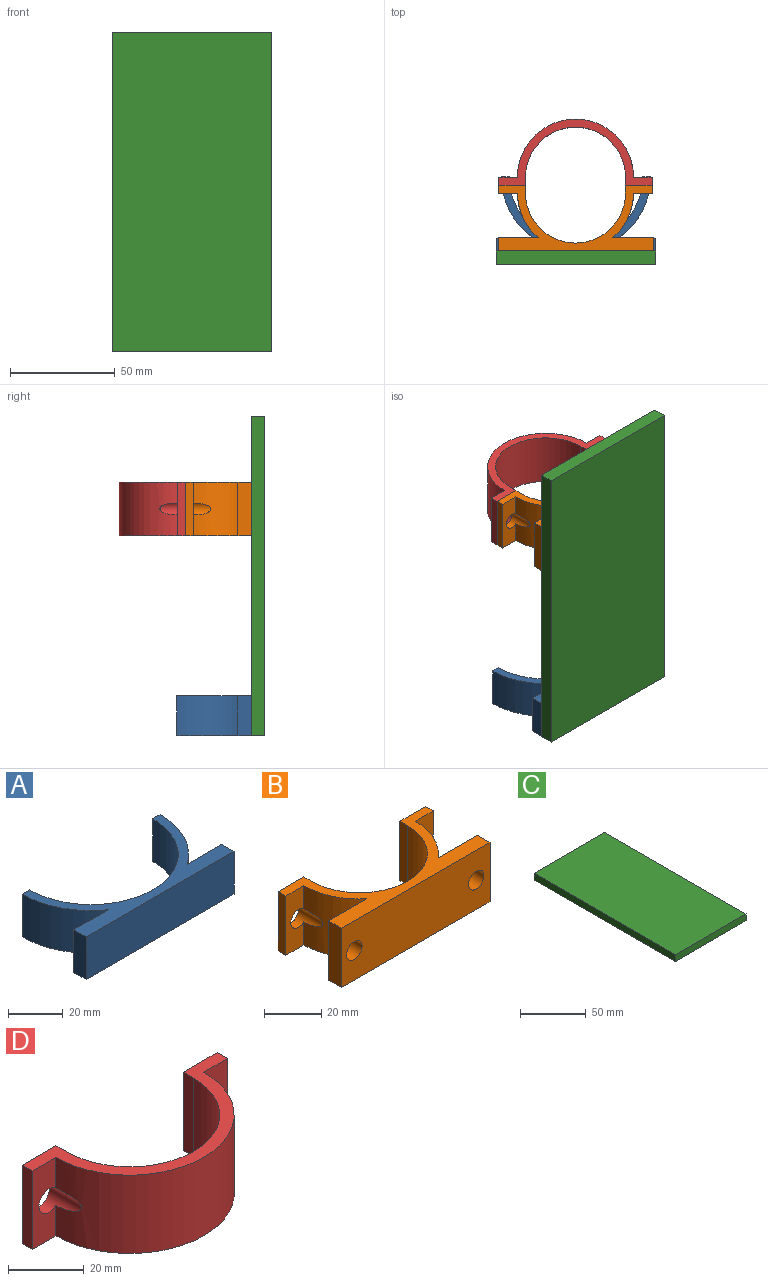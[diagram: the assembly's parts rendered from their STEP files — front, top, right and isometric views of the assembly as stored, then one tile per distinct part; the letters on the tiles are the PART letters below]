
ASSEMBLY  parts=4 mates=3
PART A: 12 faces, bbox 76.2x35.6x19.1 mm
  f0: cylinder r=31.75mm len=63.5mm, axis (0,0,-1), area 1900.2mm2, adj f1,f9,f10,f11
  f1: plane 19.05x3.81mm, normal (0,1,0), area 72.6mm2, adj f0,f2,f10,f11
  f2: cylinder r=35.56mm len=29.21mm, axis (0,0,-1), area 653mm2, adj f1,f3,f10,f11
  f3: plane 19.05x17.82mm, normal (0,1,0), area 339.5mm2, adj f2,f4,f10,f11
  f4: plane 19.05x6.35mm, normal (-1,0,0), area 121mm2, adj f3,f5,f10,f11
  f5: plane 76.2x19.05mm, normal (0,-1,0), area 1451.6mm2, adj f4,f6,f10,f11
  f6: plane 19.05x6.35mm, normal (1,0,0), area 121mm2, adj f5,f7,f10,f11
  f7: plane 19.05x17.82mm, normal (0,1,0), area 339.5mm2, adj f6,f8,f10,f11
  f8: cylinder r=35.56mm len=29.21mm, axis (0,0,-1), area 653mm2, adj f7,f9,f10,f11
  f9: plane 19.05x3.81mm, normal (0,1,0), area 72.6mm2, adj f0,f8,f10,f11
  f10: plane 76.2x35.56mm, normal (0,0,1), area 711.7mm2, adj f0,f1,f2,f3,f4,f5,f6,f7
  f11: plane 76.2x35.56mm, normal (0,0,-1), area 711.7mm2, adj f0,f1,f2,f3,f4,f5,f6,f7
PART B: 22 faces, bbox 73.5x31.4x25.4 mm
  f0: cylinder r=23.81mm len=47.63mm, axis (0,0,-1), area 1900.2mm2, adj f1,f15,f16,f17
  f1: plane 25.4x3.81mm, normal (1,0,0), area 96.8mm2, adj f0,f2,f16,f17
  f2: plane 25.4x12.7mm, normal (0,1,0), area 277mm2, adj f1,f3,f16,f17,f21
  f3: plane 25.4x3.81mm, normal (-1,0,0), area 96.8mm2, adj f2,f4,f16,f17
  f4: plane 25.4x8.89mm, normal (0,-1,0), area 185.2mm2, adj f3,f5,f16,f17,f21
  f5: cylinder r=27.62mm len=25.4mm, axis (0,0,-1), area 578.4mm2, adj f4,f6,f16,f17,f21
  f6: plane 25.4x18.89mm, normal (0,1,0), area 434.3mm2, adj f5,f7,f16,f17,f20
  f7: plane 25.4x6.35mm, normal (-1,0,0), area 161.3mm2, adj f6,f8,f16,f17
  f8: plane 73.5x25.4mm, normal (0,-1,0), area 1775.6mm2, adj f7,f9,f16,f17,f19,f20
  f9: plane 25.4x6.35mm, normal (1,0,0), area 161.3mm2, adj f8,f10,f16,f17
  f10: plane 25.4x19.36mm, normal (0,1,0), area 446.2mm2, adj f9,f11,f16,f17,f19
  f11: cylinder r=27.62mm len=25.4mm, axis (0,0,-1), area 578.3mm2, adj f10,f12,f16,f17,f18
  f12: plane 25.4x8.89mm, normal (0,-1,0), area 185.2mm2, adj f11,f13,f16,f17,f18
  f13: plane 25.4x3.81mm, normal (1,0,0), area 96.8mm2, adj f12,f14,f16,f17
  f14: plane 25.4x12.7mm, normal (0,1,0), area 277mm2, adj f13,f15,f16,f17,f18
  f15: plane 25.4x3.81mm, normal (-1,0,0), area 96.8mm2, adj f0,f14,f16,f17
  f16: plane 73.5x31.43mm, normal (0,0,1), area 718.3mm2, adj f0,f1,f2,f3,f4,f5,f6,f7
  f17: plane 73.5x31.43mm, normal (0,0,-1), area 718.3mm2, adj f0,f1,f2,f3,f4,f5,f6,f7
  f18: cylinder r=3.81mm len=12.09mm, axis (0,1,0), area 132.7mm2, adj f11,f12,f14
  f19: cylinder r=3.81mm len=7.62mm, axis (0,1,0), area 152mm2, adj f8,f10
  f20: cylinder r=3.81mm len=7.62mm, axis (0,1,0), area 152mm2, adj f6,f8
  f21: cylinder r=3.81mm len=12.09mm, axis (0,1,0), area 132.7mm2, adj f2,f4,f5
PART C: 6 faces, bbox 76.2x152.4x6.4 mm
  f0: plane 76.2x6.35mm, normal (0,-1,0), area 483.9mm2, adj f1,f3,f4,f5
  f1: plane 152.4x6.35mm, normal (1,0,0), area 967.7mm2, adj f0,f2,f4,f5
  f2: plane 76.2x6.35mm, normal (0,1,0), area 483.9mm2, adj f1,f3,f4,f5
  f3: plane 152.4x6.35mm, normal (-1,0,0), area 967.7mm2, adj f0,f2,f4,f5
  f4: plane 152.4x76.2mm, normal (0,0,1), area 11612.9mm2, adj f0,f1,f2,f3
  f5: plane 152.4x76.2mm, normal (0,0,-1), area 11612.9mm2, adj f0,f1,f2,f3
PART D: 14 faces, bbox 73x31.4x25.4 mm
  f0: plane 25.4x8.89mm, normal (0,-1,0), area 185.2mm2, adj f1,f9,f10,f11,f12
  f1: cylinder r=27.62mm len=55.25mm, axis (0,0,-1), area 2127.5mm2, adj f0,f2,f10,f11,f12,f13
  f2: plane 25.4x8.89mm, normal (0,-1,0), area 185.2mm2, adj f1,f3,f10,f11,f13
  f3: plane 25.4x3.81mm, normal (1,0,0), area 96.8mm2, adj f2,f4,f10,f11
  f4: plane 25.4x12.7mm, normal (0,1,0), area 277mm2, adj f3,f5,f10,f11,f13
  f5: plane 25.4x3.81mm, normal (-1,0,0), area 96.8mm2, adj f4,f6,f10,f11
  f6: cylinder r=23.81mm len=47.63mm, axis (0,0,-1), area 1900.2mm2, adj f5,f7,f10,f11
  f7: plane 25.4x3.81mm, normal (1,0,0), area 96.8mm2, adj f6,f8,f10,f11
  f8: plane 25.4x12.7mm, normal (0,1,0), area 277mm2, adj f7,f9,f10,f11,f12
  f9: plane 25.4x3.81mm, normal (-1,0,0), area 96.8mm2, adj f0,f8,f10,f11
  f10: plane 73.03x31.43mm, normal (0,0,1), area 404.6mm2, adj f0,f1,f2,f3,f4,f5,f6,f7
  f11: plane 73.03x31.43mm, normal (0,0,-1), area 404.6mm2, adj f0,f1,f2,f3,f4,f5,f6,f7
  f12: cylinder r=3.81mm len=12.09mm, axis (0,1,0), area 132.7mm2, adj f0,f1,f8
  f13: cylinder r=3.81mm len=12.09mm, axis (0,1,0), area 132.7mm2, adj f1,f2,f4
PLACE A t=(-46.41,-22.78,-60.73)mm
PLACE B t=(-46.65,-4.76,34.52)mm
PLACE C rot(axis=(-1,0,0),90deg) t=(-46.41,-64.69,15.29)mm
PLACE D rot(axis=(0,0,1),180deg) t=(-46.65,-23.1,34.52)mm
MATE planar C.f4 <-> B.f8  axis (0,1,0) through (-46.41,-58.34,15.29)mm
MATE fastened D.f4 <-> B.f2  axis (0,-1,0) through (-76.82,-26.91,59.92)mm
MATE planar A.f5 <-> C.f4  axis (0,-1,0) through (-46.41,-58.34,-51.21)mm
